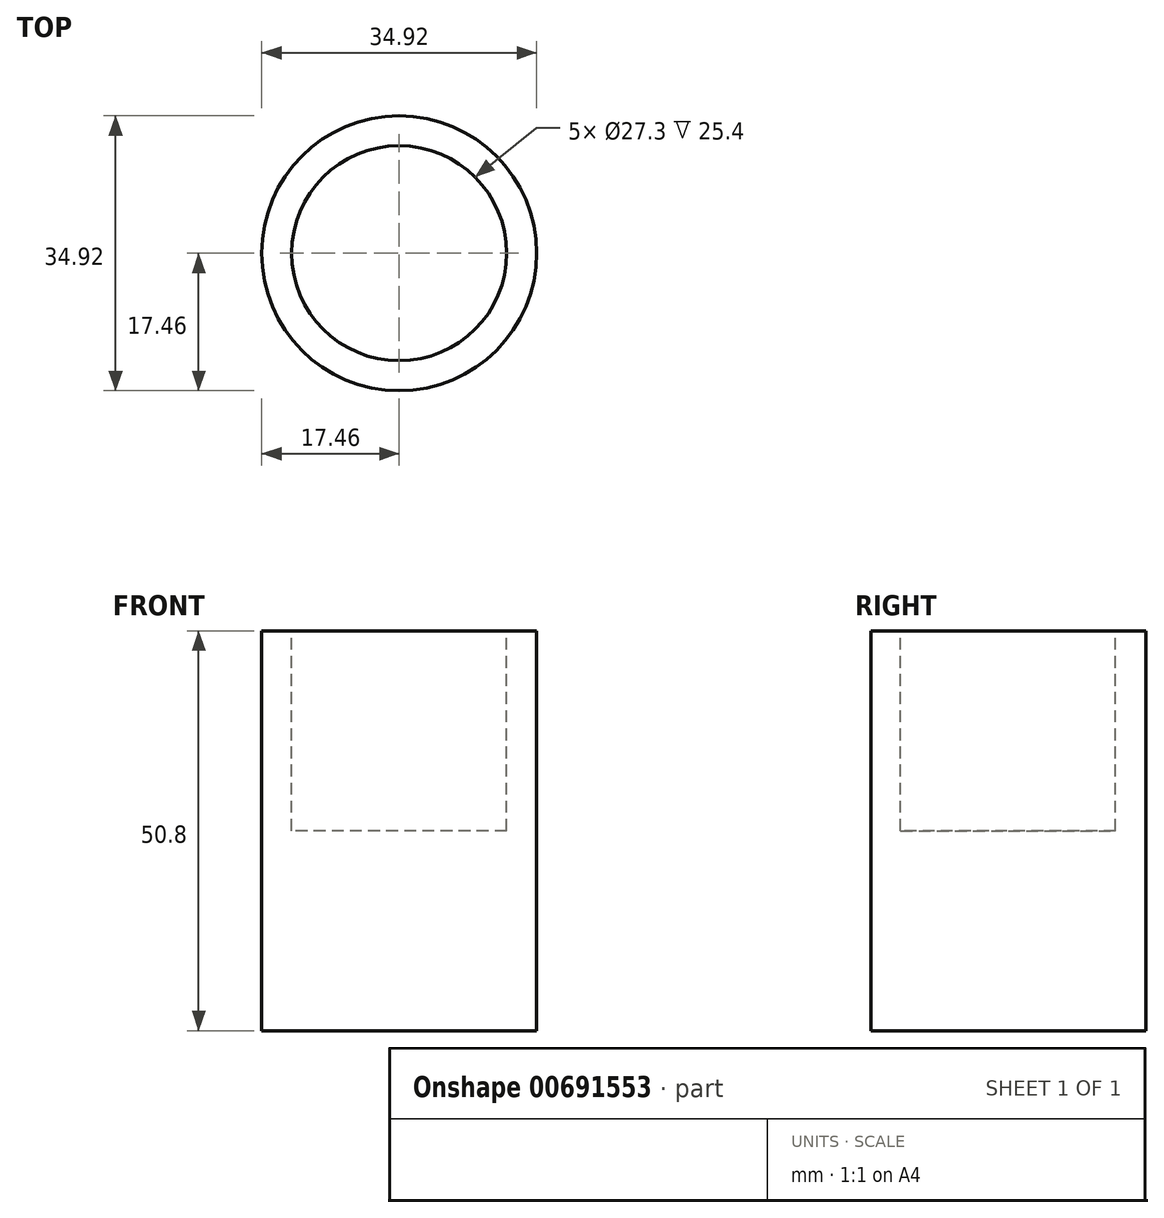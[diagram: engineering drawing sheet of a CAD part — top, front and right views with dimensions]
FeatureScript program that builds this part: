
annotation { "Feature Type Name" : "Feature", "Feature Type Description" : "" }
export const myFeature = defineFeature(function(context is Context, id is Id, definition is map)
    precondition{}
    {
        {
            var Q0;
            Q0=qCreatedBy(makeId("Top.planeOp"),FACE);
            var sketch = newSketch(context, id + "F0", { "sketchPlane" : qUnion([Q0])});
            skCircle(sketch, "E0", {"center": v(0, 0) * mm, "radius": 17.46 * mm});
            skSolve(sketch);
        }
        {
            var Q0;
            Q0 = qSketchRegion(id + "F0", true);
            var Q1;
            Q1=makeQuery(id+"F0.imprint","IMPRINT",FACE,{"disambiguationData":[TD([[makeQuery(id+"F0.imprint","IMPRINT",EDGE,{"derivedFrom":sQuery(id+"F0.wireOp",EDGE,"E0")}),1.0]])]});
            extrude(context, id + "F1", {"entities" : qUnion([Q0, Q1]), "depth" : 50.8 * mm, "offsetDistance" : 25 * mm});
        }
        {
            var Q0;
            Q0=makeQuery(id+"F1.opExtrude","CAP_FACE",FACE,{"disambiguationData":[OSD([sQuery(id+"F0.wireOp",EDGE,"E0")])],"isStart":false});
            var sketch = newSketch(context, id + "F2", { "sketchPlane" : qUnion([Q0])});
            skCircle(sketch, "E1", {"center": v(0, 0) * mm, "radius": 13.65 * mm});
            skSolve(sketch);
        }
        {
            var Q0;
            Q0=makeQuery(id+"F2.imprint","IMPRINT",FACE,{"disambiguationData":[TD([[makeQuery(id+"F2.imprint","IMPRINT",EDGE,{"derivedFrom":sQuery(id+"F2.wireOp",EDGE,"E1")}),1.0]])]});
            extrude(context, id + "F3", {"entities" : qUnion([Q0]), "operationType" : NewBodyOperationType.REMOVE, "oppositeDirection" : true, "depth" : 25.4 * mm, "offsetDistance" : 25 * mm});
        }
    });
